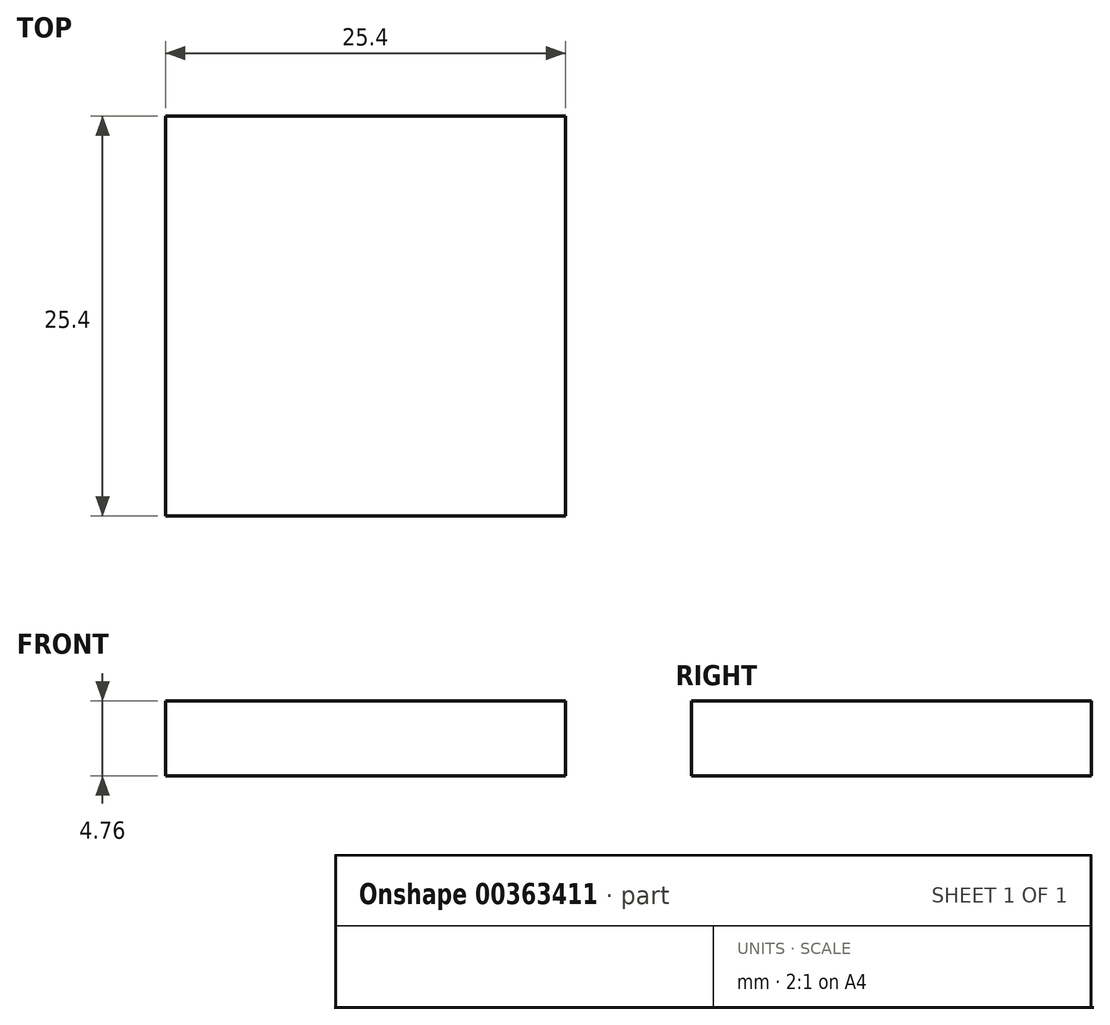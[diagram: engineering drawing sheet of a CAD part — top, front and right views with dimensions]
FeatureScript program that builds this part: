
annotation { "Feature Type Name" : "Feature", "Feature Type Description" : "" }
export const myFeature = defineFeature(function(context is Context, id is Id, definition is map)
    precondition{}
    {
        {
            var Q0;
            Q0=qCreatedBy(makeId("Top.planeOp"),FACE);
            var sketch = newSketch(context, id + "F0", { "sketchPlane" : qUnion([Q0])});
            skLineSegment(sketch, "E0.bottom", {"start": v(0, 0) * mm, "end": v(25.4, 0) * mm});
            skLineSegment(sketch, "E0.top", {"start": v(0, 25.4) * mm, "end": v(25.4, 25.4) * mm});
            skLineSegment(sketch, "E0.left", {"start": v(0, 0) * mm, "end": v(0, 25.4) * mm});
            skLineSegment(sketch, "E0.right", {"start": v(25.4, 0) * mm, "end": v(25.4, 25.4) * mm});
            skSolve(sketch);
        }
        {
            var Q0;
            Q0 = qSketchRegion(id + "F0", true);
            extrude(context, id + "F1", {"entities" : qUnion([Q0]), "depth" : 4.76 * mm});
        }
    });
